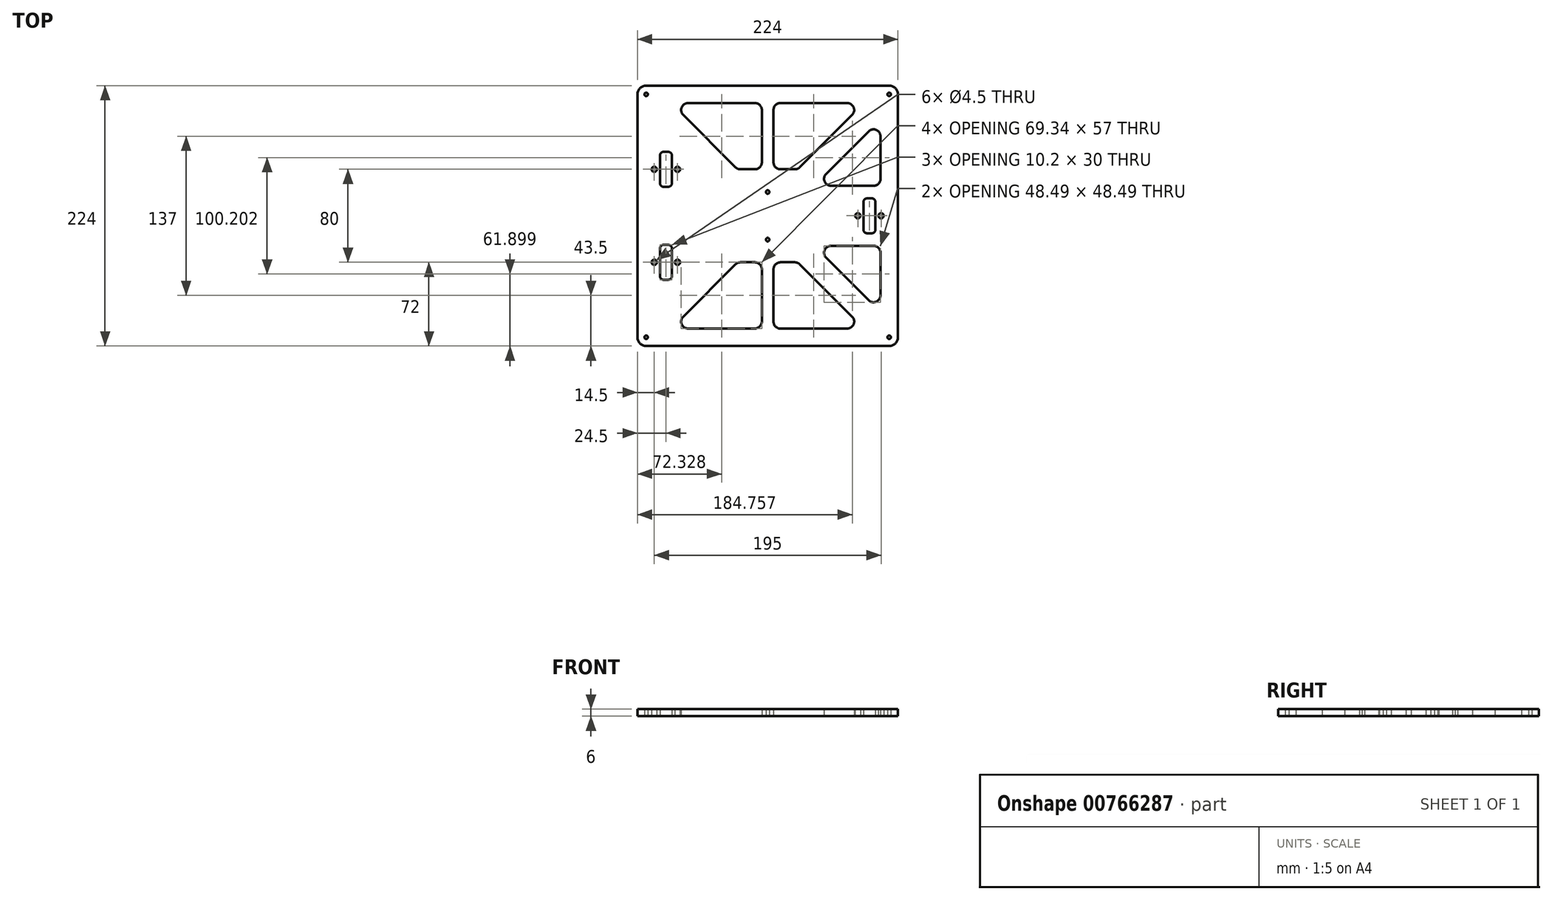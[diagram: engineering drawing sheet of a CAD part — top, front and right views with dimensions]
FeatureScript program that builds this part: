
annotation { "Feature Type Name" : "Feature", "Feature Type Description" : "" }
export const myFeature = defineFeature(function(context is Context, id is Id, definition is map)
    precondition{}
    {
        {
            var Q0;
            Q0=qCreatedBy(makeId("Top.planeOp"),FACE);
            var sketch = newSketch(context, id + "F0", { "sketchPlane" : qUnion([Q0])});
            skPoint(sketch, "E0.middle", {"position": v(0, 0) * mm});
            skCircle(sketch, "E1", {"center": v(-104.5, 104.5) * mm, "radius": 1.5 * mm});
            skCircle(sketch, "E2", {"center": v(104.5, 104.5) * mm, "radius": 1.5 * mm});
            skCircle(sketch, "E3", {"center": v(104.5, -104.5) * mm, "radius": 1.5 * mm});
            skCircle(sketch, "E4", {"center": v(-104.5, -104.5) * mm, "radius": 1.5 * mm});
            skCircle(sketch, "E5", {"center": v(0, 20.5) * mm, "radius": 1.5 * mm});
            skCircle(sketch, "E6", {"center": v(0, -20.5) * mm, "radius": 1.5 * mm});
            skLineSegment(sketch, "E7.bottom", {"start": v(89.6, 15) * mm, "end": v(85.4, 15) * mm});
            skLineSegment(sketch, "E7.top", {"start": v(89.6, -15) * mm, "end": v(85.4, -15) * mm});
            skLineSegment(sketch, "E7.left", {"start": v(92.6, 12) * mm, "end": v(92.6, -12) * mm});
            skLineSegment(sketch, "E7.right", {"start": v(82.4, 12) * mm, "end": v(82.4, -12) * mm});
            skPoint(sketch, "E7.middle", {"position": v(87.5, 0) * mm});
            skLineSegment(sketch, "E8.bottom", {"start": v(-85.4, 25) * mm, "end": v(-89.6, 25) * mm});
            skLineSegment(sketch, "E8.top", {"start": v(-85.4, 55) * mm, "end": v(-89.6, 55) * mm});
            skLineSegment(sketch, "E8.left", {"start": v(-82.4, 28) * mm, "end": v(-82.4, 52) * mm});
            skLineSegment(sketch, "E8.right", {"start": v(-92.6, 28) * mm, "end": v(-92.6, 52) * mm});
            skPoint(sketch, "E8.middle", {"position": v(-87.5, 40) * mm});
            skLineSegment(sketch, "E9.bottom", {"start": v(-85.4, -25) * mm, "end": v(-89.6, -25) * mm});
            skLineSegment(sketch, "E9.top", {"start": v(-85.4, -55) * mm, "end": v(-89.6, -55) * mm});
            skLineSegment(sketch, "E9.left", {"start": v(-82.4, -28) * mm, "end": v(-82.4, -52) * mm});
            skLineSegment(sketch, "E9.right", {"start": v(-92.6, -28) * mm, "end": v(-92.6, -52) * mm});
            skPoint(sketch, "E9.middle", {"position": v(-87.5, -40) * mm});
            skPoint(sketch, "E10.visualSharp", {"position": v(-92.6, 55) * mm});
            skArc(sketch, "E10.filletArc", {"start": v(-89.6, 55) * mm, "mid": v(-91.72, 54.12) * mm, "end": v(-92.6, 52) * mm});
            skPoint(sketch, "E11.visualSharp", {"position": v(-82.4, 55) * mm});
            skArc(sketch, "E11.filletArc", {"start": v(-82.4, 52) * mm, "mid": v(-83.28, 54.12) * mm, "end": v(-85.4, 55) * mm});
            skPoint(sketch, "E12.visualSharp", {"position": v(-82.4, 25) * mm});
            skArc(sketch, "E12.filletArc", {"start": v(-85.4, 25) * mm, "mid": v(-83.28, 25.88) * mm, "end": v(-82.4, 28) * mm});
            skPoint(sketch, "E13.visualSharp", {"position": v(-92.6, 25) * mm});
            skArc(sketch, "E13.filletArc", {"start": v(-92.6, 28) * mm, "mid": v(-91.72, 25.88) * mm, "end": v(-89.6, 25) * mm});
            skPoint(sketch, "E14.visualSharp", {"position": v(-82.4, -25) * mm});
            skArc(sketch, "E14.filletArc", {"start": v(-82.4, -28) * mm, "mid": v(-83.28, -25.88) * mm, "end": v(-85.4, -25) * mm});
            skPoint(sketch, "E15.visualSharp", {"position": v(-92.6, -25) * mm});
            skArc(sketch, "E15.filletArc", {"start": v(-89.6, -25) * mm, "mid": v(-91.72, -25.88) * mm, "end": v(-92.6, -28) * mm});
            skPoint(sketch, "E16.visualSharp", {"position": v(-92.6, -55) * mm});
            skArc(sketch, "E16.filletArc", {"start": v(-92.6, -52) * mm, "mid": v(-91.72, -54.12) * mm, "end": v(-89.6, -55) * mm});
            skPoint(sketch, "E17.visualSharp", {"position": v(-82.4, -55) * mm});
            skArc(sketch, "E17.filletArc", {"start": v(-85.4, -55) * mm, "mid": v(-83.28, -54.12) * mm, "end": v(-82.4, -52) * mm});
            skPoint(sketch, "E18.visualSharp", {"position": v(92.6, -15) * mm});
            skArc(sketch, "E18.filletArc", {"start": v(89.6, -15) * mm, "mid": v(91.72, -14.12) * mm, "end": v(92.6, -12) * mm});
            skPoint(sketch, "E19.visualSharp", {"position": v(82.4, -15) * mm});
            skArc(sketch, "E19.filletArc", {"start": v(82.4, -12) * mm, "mid": v(83.28, -14.12) * mm, "end": v(85.4, -15) * mm});
            skPoint(sketch, "E20.visualSharp", {"position": v(82.4, 15) * mm});
            skArc(sketch, "E20.filletArc", {"start": v(85.4, 15) * mm, "mid": v(83.28, 14.12) * mm, "end": v(82.4, 12) * mm});
            skPoint(sketch, "E21.visualSharp", {"position": v(92.6, 15) * mm});
            skArc(sketch, "E21.filletArc", {"start": v(92.6, 12) * mm, "mid": v(91.72, 14.12) * mm, "end": v(89.6, 15) * mm});
            skCircle(sketch, "E22", {"center": v(-77.5, 40) * mm, "radius": 2.25 * mm});
            skCircle(sketch, "E23", {"center": v(-97.5, 40) * mm, "radius": 2.25 * mm});
            skCircle(sketch, "E24", {"center": v(-77.5, -40) * mm, "radius": 2.25 * mm});
            skCircle(sketch, "E25", {"center": v(-97.5, -40) * mm, "radius": 2.25 * mm});
            skCircle(sketch, "E26", {"center": v(97.5, 0) * mm, "radius": 2.25 * mm});
            skCircle(sketch, "E27", {"center": v(77.5, 0) * mm, "radius": 2.25 * mm});
            skLineSegment(sketch, "E28.bottom", {"start": v(-104.5, 112) * mm, "end": v(104.5, 112) * mm});
            skLineSegment(sketch, "E28.top", {"start": v(-104.5, -112) * mm, "end": v(104.5, -112) * mm});
            skLineSegment(sketch, "E28.left", {"start": v(-112, 104.5) * mm, "end": v(-112, -104.5) * mm});
            skLineSegment(sketch, "E28.right", {"start": v(112, 104.5) * mm, "end": v(112, -104.5) * mm});
            skPoint(sketch, "E29.visualSharp", {"position": v(-112, 112) * mm});
            skArc(sketch, "E29.filletArc", {"start": v(-104.5, 112) * mm, "mid": v(-109.8, 109.8) * mm, "end": v(-112, 104.5) * mm});
            skPoint(sketch, "E30.visualSharp", {"position": v(112, 112) * mm});
            skArc(sketch, "E30.filletArc", {"start": v(112, 104.5) * mm, "mid": v(109.8, 109.8) * mm, "end": v(104.5, 112) * mm});
            skPoint(sketch, "E31.visualSharp", {"position": v(112, -112) * mm});
            skArc(sketch, "E31.filletArc", {"start": v(104.5, -112) * mm, "mid": v(109.8, -109.8) * mm, "end": v(112, -104.5) * mm});
            skPoint(sketch, "E32.visualSharp", {"position": v(-112, -112) * mm});
            skArc(sketch, "E32.filletArc", {"start": v(-112, -104.5) * mm, "mid": v(-109.8, -109.8) * mm, "end": v(-104.5, -112) * mm});
            skLineSegment(sketch, "E33", {"start": v(-112, 112) * mm, "end": v(112, -112) * mm, "construction": true});
            skLineSegment(sketch, "E34", {"start": v(112, 112) * mm, "end": v(-112, -112) * mm, "construction": true});
            skLineSegment(sketch, "E35.left", {"start": v(5, 91) * mm, "end": v(5, 46) * mm});
            skLineSegment(sketch, "E35.right", {"start": v(-5, 91) * mm, "end": v(-5, 46) * mm});
            skLineSegment(sketch, "E36", {"start": v(-68.37, 97) * mm, "end": v(-11, 97) * mm});
            skLineSegment(sketch, "E37", {"start": v(11, 97) * mm, "end": v(68.37, 97) * mm});
            skLineSegment(sketch, "E38", {"start": v(-11, 40) * mm, "end": v(-23.37, 40) * mm});
            skLineSegment(sketch, "E39", {"start": v(11, 40) * mm, "end": v(23.37, 40) * mm});
            skPoint(sketch, "E40.visualSharp", {"position": v(-5, 97) * mm});
            skArc(sketch, "E40.filletArc", {"start": v(-5, 91) * mm, "mid": v(-6.76, 95.24) * mm, "end": v(-11, 97) * mm});
            skPoint(sketch, "E41.visualSharp", {"position": v(-5, 40) * mm});
            skArc(sketch, "E41.filletArc", {"start": v(-11, 40) * mm, "mid": v(-6.76, 41.76) * mm, "end": v(-5, 46) * mm});
            skLineSegment(sketch, "E42", {"start": v(-72.62, 86.76) * mm, "end": v(-27.62, 41.76) * mm});
            skPoint(sketch, "E43.visualSharp", {"position": v(-25.86, 40) * mm});
            skArc(sketch, "E43.filletArc", {"start": v(-27.62, 41.76) * mm, "mid": v(-25.67, 40.46) * mm, "end": v(-23.37, 40) * mm});
            skPoint(sketch, "E44.visualSharp", {"position": v(-82.86, 97) * mm});
            skArc(sketch, "E44.filletArc", {"start": v(-68.37, 97) * mm, "mid": v(-73.92, 93.3) * mm, "end": v(-72.62, 86.76) * mm});
            skLineSegment(sketch, "E45", {"start": v(72.62, 86.76) * mm, "end": v(27.62, 41.76) * mm});
            skPoint(sketch, "E46.visualSharp", {"position": v(5, 97) * mm});
            skArc(sketch, "E46.filletArc", {"start": v(11, 97) * mm, "mid": v(6.76, 95.24) * mm, "end": v(5, 91) * mm});
            skPoint(sketch, "E47.visualSharp", {"position": v(82.86, 97) * mm});
            skArc(sketch, "E47.filletArc", {"start": v(72.62, 86.76) * mm, "mid": v(73.92, 93.3) * mm, "end": v(68.37, 97) * mm});
            skPoint(sketch, "E48.visualSharp", {"position": v(25.86, 40) * mm});
            skArc(sketch, "E48.filletArc", {"start": v(23.37, 40) * mm, "mid": v(25.67, 40.46) * mm, "end": v(27.62, 41.76) * mm});
            skPoint(sketch, "E49.visualSharp", {"position": v(5, 40) * mm});
            skArc(sketch, "E49.filletArc", {"start": v(5, 46) * mm, "mid": v(6.76, 41.76) * mm, "end": v(11, 40) * mm});
            skLineSegment(sketch, "E50", {"start": v(50.24, 36.1) * mm, "end": v(86.76, 72.62) * mm});
            skLineSegment(sketch, "E51", {"start": v(97, 68.37) * mm, "end": v(97, 31.86) * mm});
            skPoint(sketch, "E52.visualSharp", {"position": v(97, 82.86) * mm});
            skArc(sketch, "E52.filletArc", {"start": v(97, 68.37) * mm, "mid": v(93.3, 73.92) * mm, "end": v(86.76, 72.62) * mm});
            skPoint(sketch, "E53.visualSharp", {"position": v(40, 25.86) * mm});
            skLineSegment(sketch, "E54", {"start": v(86.76, -72.62) * mm, "end": v(50.24, -36.1) * mm});
            skLineSegment(sketch, "E55", {"start": v(54.49, -25.86) * mm, "end": v(91, -25.86) * mm});
            skLineSegment(sketch, "E56", {"start": v(97, -31.86) * mm, "end": v(97, -68.37) * mm});
            skLineSegment(sketch, "E57", {"start": v(54.49, 25.86) * mm, "end": v(91, 25.86) * mm});
            skPoint(sketch, "E58.visualSharp", {"position": v(97, 25.86) * mm});
            skArc(sketch, "E58.filletArc", {"start": v(91, 25.86) * mm, "mid": v(95.24, 27.62) * mm, "end": v(97, 31.86) * mm});
            skArc(sketch, "E59.filletArc", {"start": v(50.24, 36.1) * mm, "mid": v(48.94, 29.56) * mm, "end": v(54.49, 25.86) * mm});
            skPoint(sketch, "E60.visualSharp", {"position": v(97, -25.86) * mm});
            skArc(sketch, "E60.filletArc", {"start": v(97, -31.86) * mm, "mid": v(95.24, -27.62) * mm, "end": v(91, -25.86) * mm});
            skPoint(sketch, "E61.visualSharp", {"position": v(40, -25.86) * mm});
            skArc(sketch, "E61.filletArc", {"start": v(54.49, -25.86) * mm, "mid": v(48.94, -29.56) * mm, "end": v(50.24, -36.1) * mm});
            skPoint(sketch, "E62.visualSharp", {"position": v(97, -82.86) * mm});
            skArc(sketch, "E62.filletArc", {"start": v(86.76, -72.62) * mm, "mid": v(93.3, -73.92) * mm, "end": v(97, -68.37) * mm});
            skLineSegment(sketch, "E63", {"start": v(-112, 0) * mm, "end": v(112, 0) * mm, "construction": true});
            skLineSegment(sketch, "E64", {"start": v(27.62, -41.76) * mm, "end": v(72.62, -86.76) * mm});
            skLineSegment(sketch, "E65", {"start": v(-27.62, -41.76) * mm, "end": v(-72.62, -86.76) * mm});
            skLineSegment(sketch, "E66.left", {"start": v(5, -46) * mm, "end": v(5, -91) * mm});
            skLineSegment(sketch, "E66.right", {"start": v(-5, -46) * mm, "end": v(-5, -91) * mm});
            skPoint(sketch, "E66.middle", {"position": v(0, -68.5) * mm});
            skLineSegment(sketch, "E67", {"start": v(-11, -97) * mm, "end": v(-68.37, -97) * mm});
            skLineSegment(sketch, "E68", {"start": v(-11, -40) * mm, "end": v(-23.37, -40) * mm});
            skLineSegment(sketch, "E69", {"start": v(11, -97) * mm, "end": v(68.37, -97) * mm});
            skLineSegment(sketch, "E70", {"start": v(11, -40) * mm, "end": v(23.37, -40) * mm});
            skPoint(sketch, "E71.visualSharp", {"position": v(-5, -40) * mm});
            skArc(sketch, "E71.filletArc", {"start": v(-5, -46) * mm, "mid": v(-6.76, -41.76) * mm, "end": v(-11, -40) * mm});
            skPoint(sketch, "E72.visualSharp", {"position": v(-5, -97) * mm});
            skArc(sketch, "E72.filletArc", {"start": v(-11, -97) * mm, "mid": v(-6.76, -95.24) * mm, "end": v(-5, -91) * mm});
            skPoint(sketch, "E73.visualSharp", {"position": v(-25.86, -40) * mm});
            skArc(sketch, "E73.filletArc", {"start": v(-23.37, -40) * mm, "mid": v(-25.67, -40.46) * mm, "end": v(-27.62, -41.76) * mm});
            skPoint(sketch, "E74.visualSharp", {"position": v(5, -97) * mm});
            skArc(sketch, "E74.filletArc", {"start": v(5, -91) * mm, "mid": v(6.76, -95.24) * mm, "end": v(11, -97) * mm});
            skPoint(sketch, "E75.visualSharp", {"position": v(82.86, -97) * mm});
            skArc(sketch, "E75.filletArc", {"start": v(68.37, -97) * mm, "mid": v(73.92, -93.3) * mm, "end": v(72.62, -86.76) * mm});
            skPoint(sketch, "E76.visualSharp", {"position": v(25.86, -40) * mm});
            skArc(sketch, "E76.filletArc", {"start": v(27.62, -41.76) * mm, "mid": v(25.67, -40.46) * mm, "end": v(23.37, -40) * mm});
            skPoint(sketch, "E77.visualSharp", {"position": v(-82.86, -97) * mm});
            skArc(sketch, "E77.filletArc", {"start": v(-72.62, -86.76) * mm, "mid": v(-73.92, -93.3) * mm, "end": v(-68.37, -97) * mm});
            skPoint(sketch, "E78.visualSharp", {"position": v(5, -40) * mm});
            skArc(sketch, "E78.filletArc", {"start": v(11, -40) * mm, "mid": v(6.76, -41.76) * mm, "end": v(5, -46) * mm});
            skSolve(sketch);
        }
        {
            var Q0;
            Q0=makeQuery(id+"F0.imprint","IMPRINT",FACE,{"disambiguationData":[TD([[makeQuery(id+"F0.imprint","IMPRINT",EDGE,{"derivedFrom":sQuery(id+"F0.wireOp",EDGE,"E1")}),-1.0]])]});
            extrude(context, id + "F1", {"entities" : qUnion([Q0]), "depth" : 6 * mm, "offsetDistance" : 25 * mm});
        }
    });
